# Revit family: Trigon_Tables_BIM
name_source: partatom
category: Arredi
units: mm (PartAtom-declared; Revit-internal decimal feet)

## family parameters
Attiva taglio nelle viste = No
Basato su piano di lavoro = No
Condiviso = No
Numero OmniClass = 23.40.20.00
Origine composizione di rendering = Geometria famiglia
Punto di calcolo locali = No
Sempre verticale = Sì
Taglio con vuoti quando caricato = No
Titolo OmniClass = General Furniture and Specialties

## types (3) — shared parameters
AVAILABLE FINISHES = Ebonized black lacquer on Oak (EB). Raw effect lacquer on Oak (RE). Hand rubbed natural oil on Oak or Walnut (NA), or hand rubbed black oil on Walnut (BO).
BASE MATERIAL = BASSAM_FELLOWS_WALNUT
BIM BADGE = https://bim.archiproducts.com
MATERIAL DESCRIPTION = Carved, solid wood.
PRODUCT SHEET = https://www.archiproducts.com
Produttore = BassamFellows
STRUCTURE MATERIAL = BASSAM_FELLOWS_WALNUT
TECHNICAL SHEET = https://bassamfellows.com
URL = https://bassamfellows.com
zero-valued in all types: Prospetto di default

## per-type parameters (varying)
| type | CB-354 | CB-355 | CB-356 | COLLECTION | DEPTH | Descrizione | HEIGHT | Modello | WIDTH |
| CB-356 | No | No | Sì | Quad | 606 mm | Solid wood coffee table | 406 mm  [stored 1.33202 ft] | Quad Coffee Table | 933 mm |
| CB-355 | No | Sì | No | Trigon | 565 mm | Triangular solid wood coffee table | 406 mm  [stored 1.33202 ft] | Trigon Side Table | 577 mm |
| CB-354 | Sì | No | No | Trigon | 519 mm | Triangular solid wood side table | 482 mm | Trigon Side Table | 505 mm |

note: column(s) folded — value = type name in every type: PRODUCT CODE

note: [stored X ft] marks values corroborated as IEEE doubles in the binary element streams (Revit-internal decimal feet)

## geometry (parser evidence)
native form markers: Sweep x4
no freeform markers — native parametric forms only
